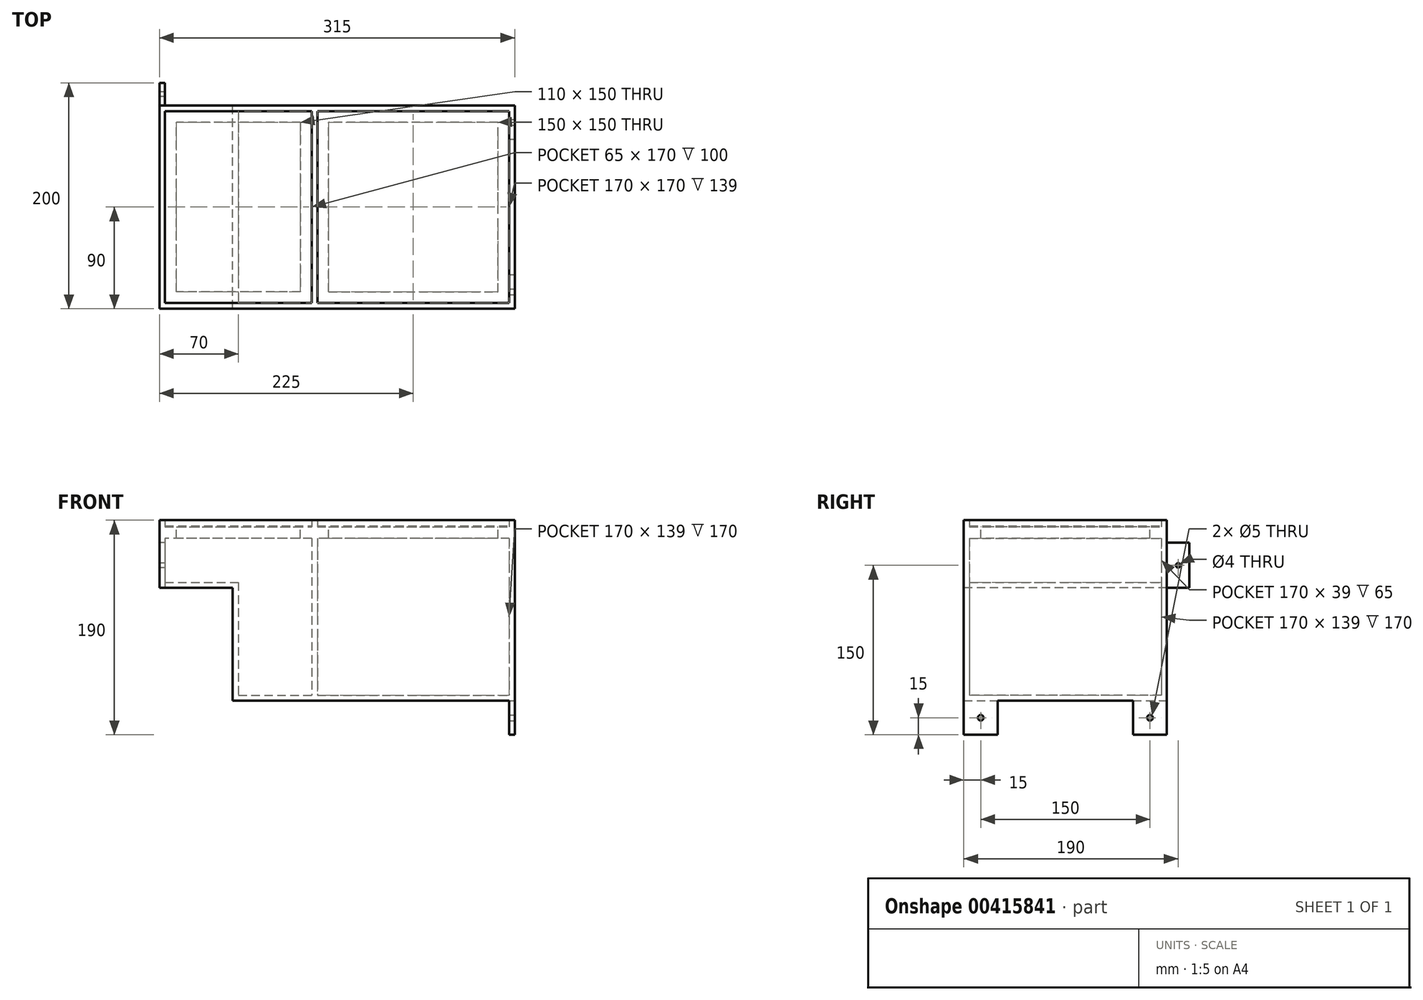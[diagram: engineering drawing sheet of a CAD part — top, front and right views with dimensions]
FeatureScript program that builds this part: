
annotation { "Feature Type Name" : "Feature", "Feature Type Description" : "" }
export const myFeature = defineFeature(function(context is Context, id is Id, definition is map)
    precondition{}
    {
        {
            var Q0;
            Q0=qCreatedBy(makeId("Top.planeOp"),FACE);
            var sketch = newSketch(context, id + "F0", { "sketchPlane" : qUnion([Q0])});
            skLineSegment(sketch, "E0.bottom", {"start": v(125, -90) * mm, "end": v(-125, -90) * mm});
            skLineSegment(sketch, "E0.top", {"start": v(125, 90) * mm, "end": v(-125, 90) * mm});
            skLineSegment(sketch, "E0.left", {"start": v(125, -90) * mm, "end": v(125, 90) * mm});
            skLineSegment(sketch, "E0.right", {"start": v(-125, -90) * mm, "end": v(-125, 90) * mm});
            skPoint(sketch, "E0.middle", {"position": v(0, 0) * mm});
            skLineSegment(sketch, "E1", {"start": v(-55, 90) * mm, "end": v(-55, -90) * mm});
            skLineSegment(sketch, "E2", {"start": v(-50, 90) * mm, "end": v(-50, -90) * mm});
            skLineSegment(sketch, "E3", {"start": v(-125, 85) * mm, "end": v(125, 85) * mm});
            skLineSegment(sketch, "E4", {"start": v(125, -85) * mm, "end": v(-125, -85) * mm});
            skLineSegment(sketch, "E5", {"start": v(120, 85) * mm, "end": v(120, -85) * mm});
            skLineSegment(sketch, "E6", {"start": v(-120, 85) * mm, "end": v(-120, -85) * mm});
            skSolve(sketch);
        }
        {
            var Q0;
            Q0=qSketchRegion(id+"F0",true);
            var Q1;
            {var subQ0=sQuery(id+"F0.wireOp",EDGE,"E3");var subQ1=sQuery(id+"F0.wireOp",EDGE,"E1");var subQ2=makeQuery(id+"F0.imprint","INTERSECT",VERTEX,{"derivedFrom":[subQ1,subQ0]});Q1=makeQuery(id+"F0.imprint","IMPRINT",FACE,{"disambiguationData":[TD([[makeQuery(id+"F0.imprint","IMPRINT",EDGE,{"disambiguationData":[TD([[subQ2,-1.0]])],"derivedFrom":subQ1}),1.0]])]});}
            extrude(context, id + "F1", {"entities" : qUnion([Q0, Q1]), "depth" : 160 * mm});
        }
        {
            var Q0;
            {var subQ5=sQuery(id+"F0.wireOp",EDGE,"E6");Q0=makeQuery(id+"F0.imprint","IMPRINT",FACE,{"disambiguationData":[TD([[makeQuery(id+"F0.imprint","IMPRINT",EDGE,{"derivedFrom":subQ5}),1.0]])]});}
            var Q1;
            {var subQ5=sQuery(id+"F0.wireOp",EDGE,"E5");Q1=makeQuery(id+"F0.imprint","IMPRINT",FACE,{"disambiguationData":[TD([[makeQuery(id+"F0.imprint","IMPRINT",EDGE,{"derivedFrom":subQ5}),-1.0]])]});}
            extrude(context, id + "F2", {"entities" : qUnion([Q0, Q1]), "operationType" : NewBodyOperationType.ADD, "depth" : 5 * mm});
        }
        {
            var Q0;
            Q0=makeQuery(id+"F1.opExtrude","SWEPT_FACE",FACE,{"disambiguationData":[OSD([sQuery(id+"F0.wireOp",EDGE,"E0.right")])]});
            var sketch = newSketch(context, id + "F3", { "sketchPlane" : qUnion([Q0])});
            skLineSegment(sketch, "E7.bottom", {"start": v(-90, 160) * mm, "end": v(90, 160) * mm});
            skLineSegment(sketch, "E7.top", {"start": v(-90, 100) * mm, "end": v(90, 100) * mm});
            skLineSegment(sketch, "E7.left", {"start": v(-90, 160) * mm, "end": v(-90, 100) * mm});
            skLineSegment(sketch, "E7.right", {"start": v(90, 160) * mm, "end": v(90, 100) * mm});
            skLineSegment(sketch, "E8", {"start": v(90, 155) * mm, "end": v(-90, 155) * mm});
            skLineSegment(sketch, "E9", {"start": v(-90, 105) * mm, "end": v(90, 105) * mm});
            skLineSegment(sketch, "E10", {"start": v(85, 155) * mm, "end": v(85, 105) * mm});
            skLineSegment(sketch, "E11", {"start": v(-85, 155) * mm, "end": v(-85, 105) * mm});
            skSolve(sketch);
        }
        {
            var Q0;
            Q0=qSketchRegion(id+"F3",true);
            var Q1;
            {var subQ0=sQuery(id+"F3.wireOp",EDGE,"E10");Q1=makeQuery(id+"F3.imprint","IMPRINT",FACE,{"disambiguationData":[TD([[makeQuery(id+"F3.imprint","IMPRINT",EDGE,{"derivedFrom":subQ0}),-1.0]])]});}
            extrude(context, id + "F4", {"entities" : qUnion([Q0, Q1]), "operationType" : NewBodyOperationType.ADD, "depth" : 65 * mm});
        }
        {
            var Q0;
            {var subQ0=sQuery(id+"F3.wireOp",EDGE,"E10");Q0=makeQuery(id+"F3.imprint","IMPRINT",FACE,{"disambiguationData":[TD([[makeQuery(id+"F3.imprint","IMPRINT",EDGE,{"derivedFrom":subQ0}),-1.0]])]});}
            extrude(context, id + "F5", {"entities" : qUnion([Q0]), "operationType" : NewBodyOperationType.REMOVE, "depth" : 60 * mm});
        }
        {
            var Q0;
            {var subQ0=sQuery(id+"F3.wireOp",EDGE,"E10");Q0=makeQuery(id+"F3.imprint","IMPRINT",FACE,{"disambiguationData":[TD([[makeQuery(id+"F3.imprint","IMPRINT",EDGE,{"derivedFrom":subQ0}),-1.0]])]});}
            extrude(context, id + "F6", {"entities" : qUnion([Q0]), "operationType" : NewBodyOperationType.REMOVE, "oppositeDirection" : true, "depth" : 6 * mm});
        }
        {
            var Q0;
            {var subQ0=sQuery(id+"F0.wireOp",EDGE,"E6");Q0=makeQuery(id+"F6.boolean.opBoolean","SPLIT",FACE,{"disambiguationData":[TD([makeQuery(id+"F4.opExtrude","SWEPT_FACE",FACE,{"disambiguationData":[OSD([sQuery(id+"F3.wireOp",EDGE,"E7.bottom")])]})])],"derivedFrom":makeQuery(id+"F1.opExtrude","SWEPT_FACE",FACE,{"disambiguationData":[OSD([subQ0])]})});}
            extrude(context, id + "F7", {"entities" : qUnion([Q0]), "operationType" : NewBodyOperationType.REMOVE, "oppositeDirection" : true, "depth" : 65 * mm});
        }
        {
            var Q0;
            Q0=makeQuery(id+"F4.opExtrude","CAP_FACE",FACE,{"disambiguationData":[OSD([sQuery(id+"F3.wireOp",EDGE,"E7.bottom"),sQuery(id+"F3.wireOp",EDGE,"E7.top"),sQuery(id+"F3.wireOp",EDGE,"E7.left"),sQuery(id+"F3.wireOp",EDGE,"E7.right")])],"isStart":false});
            var sketch = newSketch(context, id + "F8", { "sketchPlane" : qUnion([Q0])});
            skLineSegment(sketch, "E12.bottom", {"start": v(-90, 100) * mm, "end": v(-110, 100) * mm});
            skLineSegment(sketch, "E12.top", {"start": v(-90, 140) * mm, "end": v(-110, 140) * mm});
            skLineSegment(sketch, "E12.left", {"start": v(-90, 100) * mm, "end": v(-90, 140) * mm});
            skLineSegment(sketch, "E12.right", {"start": v(-110, 100) * mm, "end": v(-110, 140) * mm});
            skLineSegment(sketch, "E13", {"start": v(-110, 120) * mm, "end": v(-90, 120) * mm, "construction": true});
            skCircle(sketch, "E14", {"center": v(-100, 120) * mm, "radius": 2 * mm});
            skSolve(sketch);
        }
        {
            var Q0;
            Q0=qSketchRegion(id+"F8",true);
            extrude(context, id + "F9", {"entities" : qUnion([Q0]), "oppositeDirection" : true, "depth" : 5 * mm});
        }
        {
            var Q0;
            Q0=makeQuery(id+"F1.opExtrude","SWEPT_FACE",FACE,{"disambiguationData":[OSD([sQuery(id+"F0.wireOp",EDGE,"E0.left")])]});
            var sketch = newSketch(context, id + "F10", { "sketchPlane" : qUnion([Q0])});
            skLineSegment(sketch, "E15.bottom", {"start": v(-90, 0) * mm, "end": v(-60, 0) * mm});
            skLineSegment(sketch, "E15.top", {"start": v(-90, -30) * mm, "end": v(-60, -30) * mm});
            skLineSegment(sketch, "E15.left", {"start": v(-90, 0) * mm, "end": v(-90, -30) * mm});
            skLineSegment(sketch, "E15.right", {"start": v(-60, 0) * mm, "end": v(-60, -30) * mm});
            skLineSegment(sketch, "E16.bottom", {"start": v(90, 0) * mm, "end": v(60, 0) * mm});
            skLineSegment(sketch, "E16.top", {"start": v(90, -30) * mm, "end": v(60, -30) * mm});
            skLineSegment(sketch, "E16.left", {"start": v(90, 0) * mm, "end": v(90, -30) * mm});
            skLineSegment(sketch, "E16.right", {"start": v(60, 0) * mm, "end": v(60, -30) * mm});
            skLineSegment(sketch, "E17", {"start": v(-60, -15) * mm, "end": v(-90, -15) * mm, "construction": true});
            skLineSegment(sketch, "E18", {"start": v(90, -15) * mm, "end": v(60, -15) * mm, "construction": true});
            skCircle(sketch, "E19", {"center": v(-75, -15) * mm, "radius": 2.5 * mm});
            skCircle(sketch, "E20", {"center": v(75, -15) * mm, "radius": 2.5 * mm});
            skSolve(sketch);
        }
        {
            var Q0;
            Q0=qSketchRegion(id+"F10",true);
            extrude(context, id + "F11", {"entities" : qUnion([Q0]), "operationType" : NewBodyOperationType.ADD, "oppositeDirection" : true, "depth" : 5 * mm});
        }
        {
            var Q0;
            {var subQ0=sQuery(id+"F0.wireOp",EDGE,"E3");Q0=makeQuery(id+"F1.opExtrude","SWEPT_FACE",FACE,{"disambiguationData":[OSD([subQ0]),TDD([makeQuery(id+"F0.imprint","IMPRINT",EDGE,{"disambiguationData":[TD([[makeQuery(id+"F0.imprint","INTERSECT",VERTEX,{"derivedFrom":[subQ0,sQuery(id+"F0.wireOp",EDGE,"E5")]}),1.0]])],"derivedFrom":subQ0})])]});}
            var sketch = newSketch(context, id + "F12", { "sketchPlane" : qUnion([Q0])});
            skLineSegment(sketch, "E21", {"start": v(-50, 154) * mm, "end": v(120, 154) * mm});
            skLineSegment(sketch, "E22", {"start": v(120, 144) * mm, "end": v(-50, 144) * mm});
            skSolve(sketch);
        }
        {
            var Q0;
            {var subQ0=sQuery(id+"F12.wireOp",EDGE,"E21");Q0=makeQuery(id+"F12.imprint","IMPRINT",FACE,{"disambiguationData":[TD([[makeQuery(id+"F12.imprint","IMPRINT",EDGE,{"derivedFrom":subQ0}),-1.0]])]});}
            extrude(context, id + "F13", {"entities" : qUnion([Q0]), "operationType" : NewBodyOperationType.ADD, "depth" : 170 * mm});
        }
        {
            var Q0;
            Q0=makeQuery(id+"F13.opExtrude","SWEPT_FACE",FACE,{"disambiguationData":[OSD([sQuery(id+"F12.wireOp",EDGE,"E21")])]});
            var sketch = newSketch(context, id + "F14", { "sketchPlane" : qUnion([Q0])});
            skLineSegment(sketch, "E23", {"start": v(-50, 75) * mm, "end": v(120, 75) * mm});
            skLineSegment(sketch, "E24", {"start": v(120, -75) * mm, "end": v(-50, -75) * mm});
            skLineSegment(sketch, "E25", {"start": v(110, 75) * mm, "end": v(110, -75) * mm});
            skLineSegment(sketch, "E26", {"start": v(-40, 75) * mm, "end": v(-40, -75) * mm});
            skSolve(sketch);
        }
        {
            var Q0;
            {var subQ0=sQuery(id+"F14.wireOp",EDGE,"E25");Q0=makeQuery(id+"F14.imprint","IMPRINT",FACE,{"disambiguationData":[TD([[makeQuery(id+"F14.imprint","IMPRINT",EDGE,{"derivedFrom":subQ0}),-1.0]])]});}
            extrude(context, id + "F15", {"entities" : qUnion([Q0]), "operationType" : NewBodyOperationType.REMOVE, "oppositeDirection" : true, "depth" : 11 * mm});
        }
        {
            var Q0;
            {var subQ0=sQuery(id+"F0.wireOp",EDGE,"E6");var subQ1=sQuery(id+"F0.wireOp",EDGE,"E3");var subQ2=sQuery(id+"F3.wireOp",EDGE,"E11");Q0=makeQuery(id+"F7.boolean.opBoolean","MERGE",FACE,{"derivedFrom":[makeQuery(id+"F6.boolean.opBoolean","MERGE",FACE,{"derivedFrom":[makeQuery(id+"F1.opExtrude","SWEPT_FACE",FACE,{"disambiguationData":[OSD([subQ1]),TDD([makeQuery(id+"F0.imprint","IMPRINT",EDGE,{"disambiguationData":[TD([[makeQuery(id+"F0.imprint","INTERSECT",VERTEX,{"derivedFrom":[subQ1,subQ0]}),-1.0]])],"derivedFrom":subQ1})])]}),makeQuery(id+"F5.boolean.opBoolean","COPY",FACE,{"derivedFrom":makeQuery(id+"F5.opExtrude","SWEPT_FACE",FACE,{"disambiguationData":[OSD([subQ2])]})}),makeQuery(id+"F6.opExtrude","SWEPT_FACE",FACE,{"disambiguationData":[OSD([subQ2])]})]}),makeQuery(id+"F7.opExtrude","SWEPT_FACE",FACE,{"disambiguationData":[OSD([subQ1,subQ0])]})]});}
            var sketch = newSketch(context, id + "F16", { "sketchPlane" : qUnion([Q0])});
            skLineSegment(sketch, "E27", {"start": v(-185, 154) * mm, "end": v(-55, 154) * mm});
            skLineSegment(sketch, "E28", {"start": v(-55, 144) * mm, "end": v(-185, 144) * mm});
            skSolve(sketch);
        }
        {
            var Q0;
            {var subQ0=sQuery(id+"F16.wireOp",EDGE,"E27");Q0=makeQuery(id+"F16.imprint","IMPRINT",FACE,{"disambiguationData":[TD([[makeQuery(id+"F16.imprint","IMPRINT",EDGE,{"derivedFrom":subQ0}),-1.0]])]});}
            extrude(context, id + "F17", {"entities" : qUnion([Q0]), "operationType" : NewBodyOperationType.ADD, "depth" : 170 * mm});
        }
        {
            var Q0;
            Q0=makeQuery(id+"F17.opExtrude","SWEPT_FACE",FACE,{"disambiguationData":[OSD([sQuery(id+"F16.wireOp",EDGE,"E27")])]});
            var sketch = newSketch(context, id + "F18", { "sketchPlane" : qUnion([Q0])});
            skLineSegment(sketch, "E29", {"start": v(-185, 75) * mm, "end": v(-55, 75) * mm});
            skLineSegment(sketch, "E30", {"start": v(-185, -75) * mm, "end": v(-55, -75) * mm});
            skLineSegment(sketch, "E31", {"start": v(-65, -75) * mm, "end": v(-65, 75) * mm});
            skLineSegment(sketch, "E32", {"start": v(-175, 75) * mm, "end": v(-175, -75) * mm});
            skSolve(sketch);
        }
        {
            var Q0;
            {var subQ0=sQuery(id+"F18.wireOp",EDGE,"E31");Q0=makeQuery(id+"F18.imprint","IMPRINT",FACE,{"disambiguationData":[TD([[makeQuery(id+"F18.imprint","IMPRINT",EDGE,{"derivedFrom":subQ0}),1.0]])]});}
            extrude(context, id + "F19", {"entities" : qUnion([Q0]), "operationType" : NewBodyOperationType.REMOVE, "oppositeDirection" : true, "depth" : 11 * mm});
        }
        {
            var Q0;
            {var subQ0=sQuery(id+"F0.wireOp",EDGE,"E5");var subQ2=sQuery(id+"F0.wireOp",EDGE,"E3");Q0=makeQuery(id+"F13.boolean.opBoolean","SPLIT",FACE,{"disambiguationData":[TD([makeQuery(id+"F4.opExtrude","SWEPT_FACE",FACE,{"disambiguationData":[OSD([sQuery(id+"F3.wireOp",EDGE,"E7.bottom")])]})])],"derivedFrom":makeQuery(id+"F1.opExtrude","SWEPT_FACE",FACE,{"disambiguationData":[OSD([subQ2]),TDD([makeQuery(id+"F0.imprint","IMPRINT",EDGE,{"disambiguationData":[TD([[makeQuery(id+"F0.imprint","INTERSECT",VERTEX,{"derivedFrom":[subQ2,subQ0]}),1.0]])],"derivedFrom":subQ2})])]})});}
            var sketch = newSketch(context, id + "F20", { "sketchPlane" : qUnion([Q0])});
            skLineSegment(sketch, "E33.bottom", {"start": v(-50, 160) * mm, "end": v(120, 160) * mm});
            skLineSegment(sketch, "E33.top", {"start": v(-50, 155) * mm, "end": v(120, 155) * mm});
            skLineSegment(sketch, "E33.left", {"start": v(-50, 160) * mm, "end": v(-50, 155) * mm});
            skLineSegment(sketch, "E33.right", {"start": v(120, 160) * mm, "end": v(120, 155) * mm});
            skSolve(sketch);
        }
        {
            var Q0;
            Q0=makeQuery(id+"F20.imprint","IMPRINT",FACE,{"disambiguationData":[TD([[makeQuery(id+"F20.imprint","IMPRINT",EDGE,{"derivedFrom":sQuery(id+"F20.wireOp",EDGE,"E33.bottom")}),-1.0]])]});
            extrude(context, id + "F21", {"entities" : qUnion([Q0]), "depth" : 170 * mm});
        }
        {
            var Q0;
            {var subQ0=sQuery(id+"F3.wireOp",EDGE,"E11");var subQ2=sQuery(id+"F0.wireOp",EDGE,"E6");var subQ3=sQuery(id+"F0.wireOp",EDGE,"E3");Q0=makeQuery(id+"F17.boolean.opBoolean","SPLIT",FACE,{"disambiguationData":[TD([makeQuery(id+"F4.opExtrude","SWEPT_FACE",FACE,{"disambiguationData":[OSD([sQuery(id+"F3.wireOp",EDGE,"E7.bottom")])]})])],"derivedFrom":makeQuery(id+"F7.boolean.opBoolean","MERGE",FACE,{"derivedFrom":[makeQuery(id+"F6.boolean.opBoolean","MERGE",FACE,{"derivedFrom":[makeQuery(id+"F1.opExtrude","SWEPT_FACE",FACE,{"disambiguationData":[OSD([subQ3]),TDD([makeQuery(id+"F0.imprint","IMPRINT",EDGE,{"disambiguationData":[TD([[makeQuery(id+"F0.imprint","INTERSECT",VERTEX,{"derivedFrom":[subQ3,subQ2]}),-1.0]])],"derivedFrom":subQ3})])]}),makeQuery(id+"F5.boolean.opBoolean","COPY",FACE,{"derivedFrom":makeQuery(id+"F5.opExtrude","SWEPT_FACE",FACE,{"disambiguationData":[OSD([subQ0])]})}),makeQuery(id+"F6.opExtrude","SWEPT_FACE",FACE,{"disambiguationData":[OSD([subQ0])]})]}),makeQuery(id+"F7.opExtrude","SWEPT_FACE",FACE,{"disambiguationData":[OSD([subQ3,subQ2])]})]})});}
            var sketch = newSketch(context, id + "F22", { "sketchPlane" : qUnion([Q0])});
            skLineSegment(sketch, "E34.bottom", {"start": v(-185, 160) * mm, "end": v(-55, 160) * mm});
            skLineSegment(sketch, "E34.top", {"start": v(-185, 155) * mm, "end": v(-55, 155) * mm});
            skLineSegment(sketch, "E34.left", {"start": v(-185, 160) * mm, "end": v(-185, 155) * mm});
            skLineSegment(sketch, "E34.right", {"start": v(-55, 160) * mm, "end": v(-55, 155) * mm});
            skSolve(sketch);
        }
        {
            var Q0;
            Q0=makeQuery(id+"F22.imprint","IMPRINT",FACE,{"disambiguationData":[TD([[makeQuery(id+"F22.imprint","IMPRINT",EDGE,{"derivedFrom":sQuery(id+"F22.wireOp",EDGE,"E34.bottom")}),-1.0]])]});
            extrude(context, id + "F23", {"entities" : qUnion([Q0]), "depth" : 170 * mm});
        }
    });
